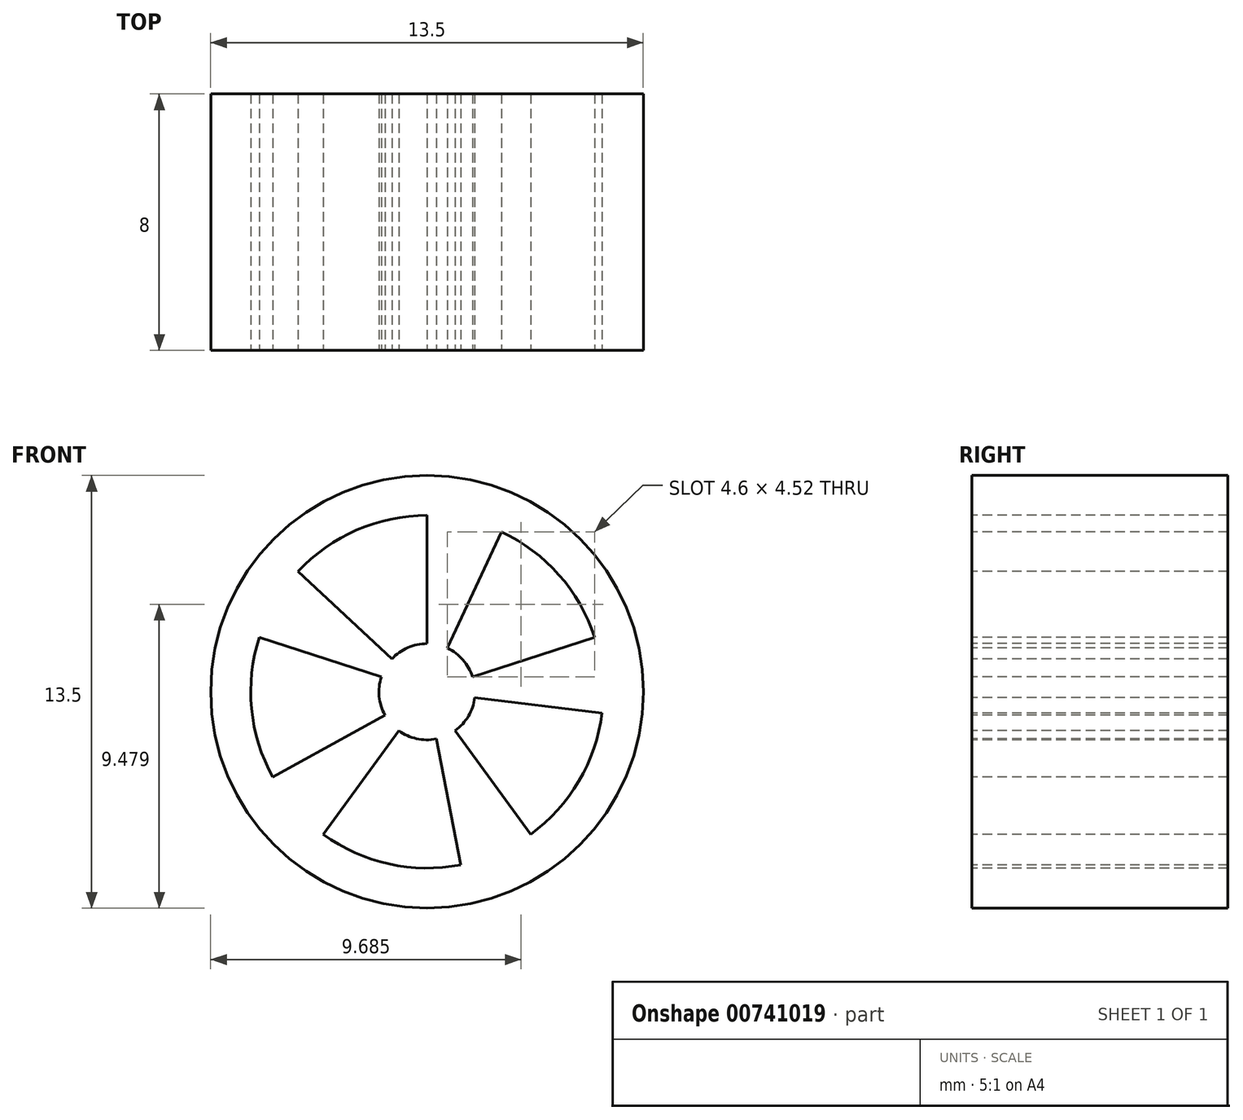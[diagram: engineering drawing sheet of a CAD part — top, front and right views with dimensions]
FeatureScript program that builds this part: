
annotation { "Feature Type Name" : "Feature", "Feature Type Description" : "" }
export const myFeature = defineFeature(function(context is Context, id is Id, definition is map)
    precondition{}
    {
        {
            var Q0;
            Q0=qCreatedBy(makeId("Front.planeOp"),FACE);
            var sketch = newSketch(context, id + "F0", { "sketchPlane" : qUnion([Q0])});
            skCircle(sketch, "E0", {"center": v(-22.47, 19.05) * mm, "radius": 6.75 * mm});
            skSolve(sketch);
        }
        {
            var Q0;
            Q0=makeQuery(id+"F0.imprint","IMPRINT",FACE,{"disambiguationData":[TD([[makeQuery(id+"F0.imprint","IMPRINT",EDGE,{"derivedFrom":sQuery(id+"F0.wireOp",EDGE,"E0")}),1.0]])]});
            extrude(context, id + "F1", {"entities" : qUnion([Q0]), "depth" : 8 * mm, "offsetDistance" : 25.4 * mm});
        }
        {
            var Q0;
            Q0=makeQuery(id+"F1.opExtrude","CAP_FACE",FACE,{"disambiguationData":[OSD([sQuery(id+"F0.wireOp",EDGE,"E0")])],"isStart":false});
            var sketch = newSketch(context, id + "F2", { "sketchPlane" : qUnion([Q0])});
            skCircle(sketch, "E1", {"center": v(-22.47, 19.05) * mm, "radius": 5.5 * mm});
            skCircle(sketch, "E2", {"center": v(-22.47, 19.05) * mm, "radius": 1.5 * mm});
            skLineSegment(sketch, "E3", {"start": v(-22.47, 20.55) * mm, "end": v(-22.47, 24.55) * mm});
            skLineSegment(sketch, "E4", {"start": v(-21.83, 20.41) * mm, "end": v(-20.14, 24.04) * mm});
            skLineSegment(sketch, "E5.1.0", {"start": v(-23.9, 19.52) * mm, "end": v(-27.7, 20.75) * mm});
            skLineSegment(sketch, "E5.1.1", {"start": v(-23.56, 20.08) * mm, "end": v(-26.49, 22.8) * mm});
            skLineSegment(sketch, "E5.2.0", {"start": v(-23.35, 17.84) * mm, "end": v(-25.7, 14.6) * mm});
            skLineSegment(sketch, "E5.2.1", {"start": v(-23.78, 18.33) * mm, "end": v(-27.28, 16.39) * mm});
            skLineSegment(sketch, "E5.3.0", {"start": v(-21.59, 17.84) * mm, "end": v(-19.23, 14.6) * mm});
            skLineSegment(sketch, "E5.3.1", {"start": v(-22.18, 17.58) * mm, "end": v(-21.42, 13.66) * mm});
            skLineSegment(sketch, "E5.4.0", {"start": v(-21.04, 19.52) * mm, "end": v(-17.24, 20.75) * mm});
            skLineSegment(sketch, "E5.4.1", {"start": v(-20.98, 18.87) * mm, "end": v(-17, 18.38) * mm});
            skSolve(sketch);
        }
        {
            var Q0;
            {var subQ0=sQuery(id+"F2.wireOp",EDGE,"E3");Q0=makeQuery(id+"F2.imprint","IMPRINT",FACE,{"disambiguationData":[TD([[makeQuery(id+"F2.imprint","IMPRINT",EDGE,{"derivedFrom":subQ0}),1.0]])]});}
            var Q1;
            {var subQ0=sQuery(id+"F2.wireOp",EDGE,"E4");Q1=makeQuery(id+"F2.imprint","IMPRINT",FACE,{"disambiguationData":[TD([[makeQuery(id+"F2.imprint","IMPRINT",EDGE,{"derivedFrom":subQ0}),-1.0]])]});}
            var Q2;
            {var subQ0=sQuery(id+"F2.wireOp",EDGE,"E5.3.0");Q2=makeQuery(id+"F2.imprint","IMPRINT",FACE,{"disambiguationData":[TD([[makeQuery(id+"F2.imprint","IMPRINT",EDGE,{"derivedFrom":subQ0}),1.0]])]});}
            var Q3;
            {var subQ0=sQuery(id+"F2.wireOp",EDGE,"E5.2.0");Q3=makeQuery(id+"F2.imprint","IMPRINT",FACE,{"disambiguationData":[TD([[makeQuery(id+"F2.imprint","IMPRINT",EDGE,{"derivedFrom":subQ0}),1.0]])]});}
            var Q4;
            {var subQ0=sQuery(id+"F2.wireOp",EDGE,"E5.1.0");Q4=makeQuery(id+"F2.imprint","IMPRINT",FACE,{"disambiguationData":[TD([[makeQuery(id+"F2.imprint","IMPRINT",EDGE,{"derivedFrom":subQ0}),1.0]])]});}
            extrude(context, id + "F3", {"entities" : qUnion([Q0, Q1, Q2, Q3, Q4]), "operationType" : NewBodyOperationType.REMOVE, "endBound" : BoundingType.THROUGH_ALL, "oppositeDirection" : true, "depth" : 25.4 * mm, "offsetDistance" : 25.4 * mm});
        }
    });
